# Revit family: Секция форсуночного орошения AIRNED-M U1
name_source: partatom
category: Оборудование
revit_build: Autodesk Revit 2017 (Build: 20160225_1515(x64)
units: mm (PartAtom-declared; Revit-internal decimal feet)

## family parameters
Всегда вертикально = Да
На основе рабочей плоскости = Нет
Общий = Нет
При загрузке вырезать с полостями = Нет
Размер круглого соединителя = Использовать диаметр
Тип детали = Нормальный
Точка расчета площади = Нет

## types (6) — shared parameters
D слива и перелива = 25 мм
d подвода = 19 мм
h = 410 мм
Д = 2150 мм
Д1 = 2130 мм
Д2 = 213 мм
Д3 = 426 мм
Д4 = 320 мм
Единица измерения = шт.
Завод изготовитель = NED
Ключевая пометка = Вентиляция
Материал = Сталь серая
Наименование и тех.хар-ка = Секция сотового увлажнения
Напряжение U,В = 3-380
Раздел = ОВ
Эффективность увлажнения, % = 95
высота ножек = 400 мм

## per-type parameters (varying)
| type | А | А1 | Б | Б1 | Высота | Мощность насоса, Вт | Размер В | Середина | Сила тока J, А | Ширина |
| AIRNED-M 6 U1.1 | 1100 мм | 1080 мм | 1100 мм | 1080 мм | 1025 мм | 3000 Вт | 385 мм | 950 мм | 6.7 | 1025 мм |
| AIRNED-M 7 U1.1 | 1100 мм | 1080 мм | 1320 мм | 1300 мм | 1245 мм | 4000 Вт | 385 мм | 1060 мм | 8.7 | 1025 мм |
| AIRNED-M 8 U1.1 | 1320 мм | 1300 мм | 1320 мм | 1300 мм | 1245 мм | 4000 Вт | 385 мм | 1060 мм | 8.7 | 1245 мм |
| AIRNED-M 12 U1.1 | 1435 мм | 1415 мм | 1435 мм | 1415 мм | 1360 мм | 5500 Вт | 385 мм | 1118 мм | 11.6 | 1360 мм |
| AIRNED-M 20 U1.1 | 1660 мм | 1640 мм | 1660 мм | 1640 мм | 1585 мм | 5500 Вт | 385 мм | 1230 мм | 11.6 | 1585 мм |
| AIRNED-M 25 U1.1 | 2045 мм | 2025 мм | 2045 мм | 2025 мм | 1970 мм | 7500 Вт | 445 мм | 1423 мм | 14 | 1970 мм |

note: column(s) folded — value = type name in every type: Тип, марка, обозначение
